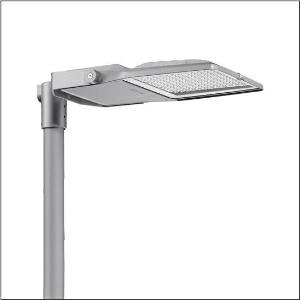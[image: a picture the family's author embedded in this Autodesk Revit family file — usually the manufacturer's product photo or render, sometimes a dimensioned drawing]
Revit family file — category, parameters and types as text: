
# Revit family: floodlight_fl_21_iq_midi___pl52_5xa7782e2d3a_7997
name_source: partatom
category: Lighting Fixtures
units: mm (PartAtom-declared; Revit-internal decimal feet)

## family parameters
Cut with Voids When Loaded = No
Host = Face
Light Source = No
Part Type = Normal
Room Calculation Point = No
Round Connector Dimension = Use Diameter
Shared = No

## types (1)
- --- (1 x LED, 26850 lm, 208.1 W, 3000K)
    Apparent Load = 208 VA
    CIE Flux Codes = 26 60 98 100 100
    Color Rendering = 70
    Color Temperature = 3000K
    Default Elevation = 1800 mm
    Description = Floodlight FL 21 iQ midi, floodlight, primary light control with lens, of PMMA, primary optical cover: protective disc, of toughened safety glass, transparent, light distribution: PL52, light emission: direct distribution, installation type: surface-mounted, LED, High Power LED, rated luminous flux: 26.850lm, luminous efficacy: 129lm/W, light colour: 730, colour temperature: 3000K, control gear: ECG iQ, control: optimised constant luminous flux control (CLO 2.0), Desk-Remote (wireless, voltage-free reading and setting of iQ features in the workshop via application-optimized NFC function/RFID function), Smart-Wire, Night-Set, Temp-Guard, Auto-Match, Street-Remote, with terminal, 6-pole, mains connection: 220..240V, AC, 50/60Hz, start of lifetime: 208W, end of service life: 227W, reduction: 90W, luminaire housing, of diecast aluminium, powder-coated, Siteco® metallic grey (DB 702S), corrosivity category C5 mid according to DIN EN ISO 12944, sealing non-destructively replaceable, please order mast flange separately, mast bracket, of steel, galvanised, powder-coated, Siteco® metallic grey (DB 702S), protection rating (complete): IP66, insulation class (complete): insulation class II (safety insulation), certification: CE, ENEC, VDE, protection symbol: D, impact resistance: IK08, permissible operating ambient temperature: -40..+40°C, permissible operating ambient temperature for outdoor applications: -40..+50°C, standard: DIN EN 12944, LABS conformity tested according to VDMA 24364:2018-05, packaging unit: 1 piece

Light Distribution: PL52
    Height = 76 mm
    Lamp = 1 x LED
    Lamp Light Flux = 26850 lm
    Lamp Power = 208.1 W
    Lamp count = 1
    Length = 657 mm
    Luminous efficacy = 129 lm/W
    Manufacturer = Siteco
    ModVariant = No
    Model = 5XA7782E2D3A
    Number of Poles = 1
    OnlyDefault = Yes
    Power Factor = 1
    Product Name = Floodlight FL 21 iQ midi | PL52
    Product group = floodlight | pylon annexe
    ProductGroupID = 6200
    Protection Class = Protection class II
    Protection Degree = IP 66
    RLX_Detail_Level = 1
    RLX_Emergency_Light_Flux = 0 lm
    RLX_Emergency_Type = 0
    RLX_Emergency_Type_DB = No
    RlxData = <blob elided: 153817 chars, md5=af3fd702>
    Socket = socket
    Standby Power = 0 W
    System Light Flux = 26850 lm
    System Power = 208 W
    Type Comments = factory setting: luminous flux: 100 % | dim-lin: 254 | 710 mA
    Type Image = l_1007123.jpg
    URL = http://relux.com
    VarID = @adj_074933
    Voltage = 0 V
    Weight = 0.00 kg
    Width = 442 mm

## geometry (parser evidence)
native form markers: Blend x4, Sweep x12
no freeform markers — native parametric forms only
